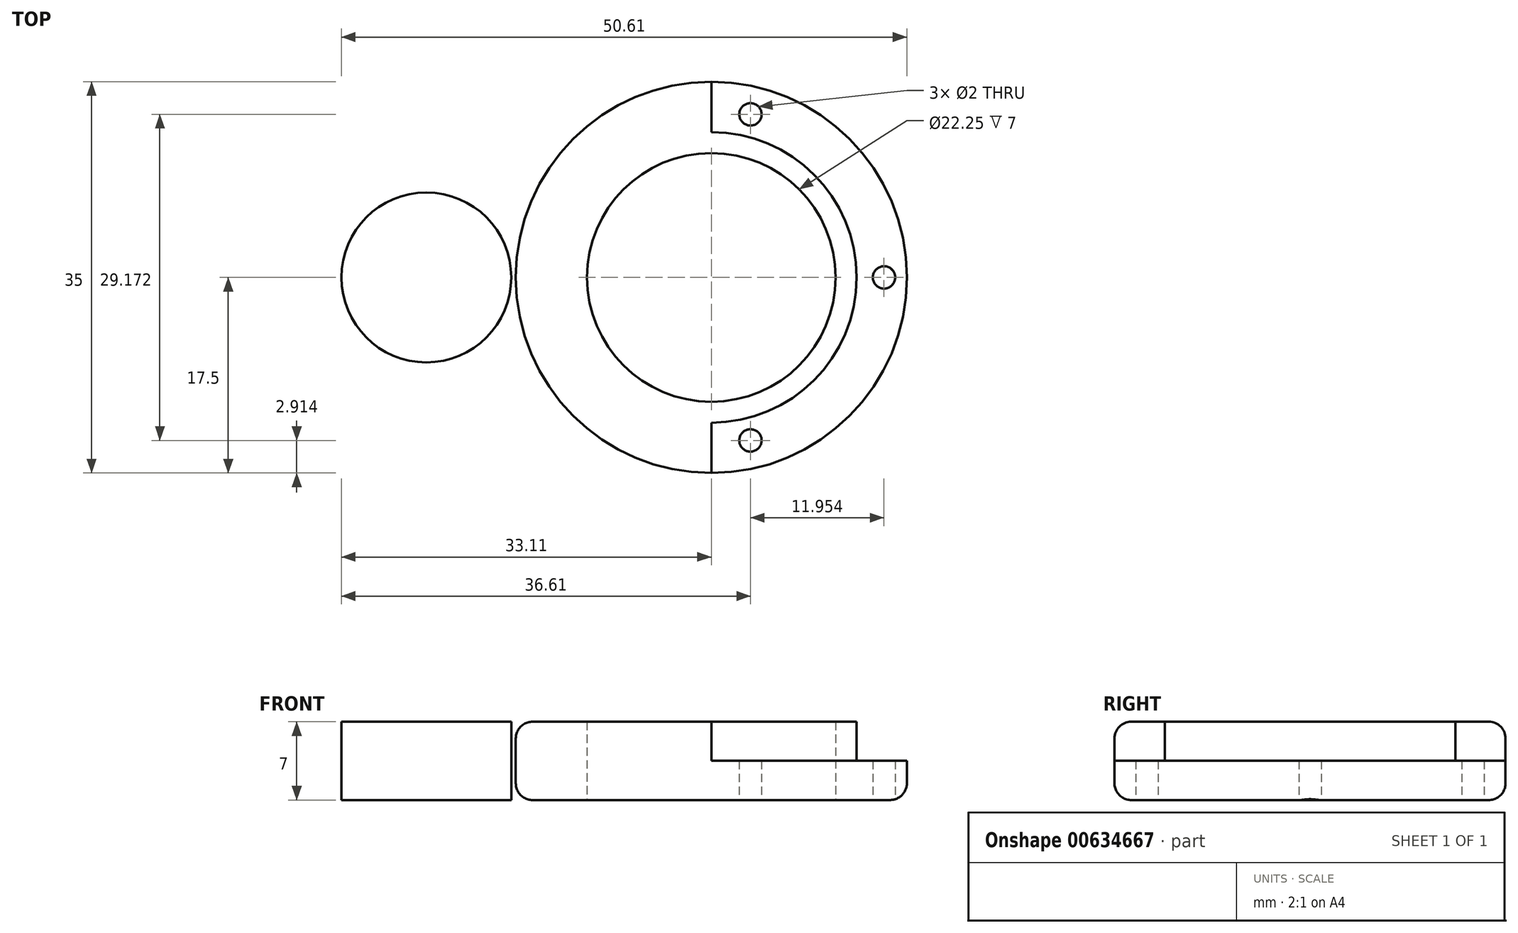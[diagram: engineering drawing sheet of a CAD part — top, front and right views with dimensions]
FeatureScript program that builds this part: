
annotation { "Feature Type Name" : "Feature", "Feature Type Description" : "" }
export const myFeature = defineFeature(function(context is Context, id is Id, definition is map)
    precondition{}
    {
        {
            var Q0;
            Q0=qCreatedBy(makeId("Top.planeOp"),FACE);
            var sketch = newSketch(context, id + "F0", { "sketchPlane" : qUnion([Q0])});
            skCircle(sketch, "E0", {"center": v(0, 0) * mm, "radius": 11.12 * mm});
            skCircle(sketch, "E1", {"center": v(0, 0) * mm, "radius": 17.5 * mm});
            skLineSegment(sketch, "E2", {"start": v(0, 0) * mm, "end": v(34.83, 0) * mm, "construction": true});
            skCircle(sketch, "E3", {"center": v(25.5, 0) * mm, "radius": 7.6 * mm});
            skArc(sketch, "E4", {"start": v(21.65, -11.36) * mm, "mid": v(37.5, 0) * mm, "end": v(21.65, 11.36) * mm});
            skArc(sketch, "E5", {"start": v(23.21, -11.78) * mm, "mid": v(17.5, -11.12) * mm, "end": v(11.98, -12.75) * mm});
            skArc(sketch, "E6.MirrorCS", {"start": v(23.21, 11.78) * mm, "mid": v(17.5, 11.12) * mm, "end": v(11.98, 12.75) * mm});
            skLineSegment(sketch, "E7.MirrorCS", {"start": v(0, 0) * mm, "end": v(-34.83, 0) * mm, "construction": true});
            skCircle(sketch, "E8.MirrorC", {"center": v(-25.5, 0) * mm, "radius": 7.6 * mm});
            skArc(sketch, "E9.MirrorC", {"start": v(-21.65, -11.36) * mm, "mid": v(-37.5, 0) * mm, "end": v(-21.65, 11.36) * mm});
            skArc(sketch, "E10.MirrorCS", {"start": v(-23.21, -11.78) * mm, "mid": v(-17.5, -11.12) * mm, "end": v(-11.98, -12.75) * mm});
            skArc(sketch, "E11.MirrorCS", {"start": v(-23.21, 11.78) * mm, "mid": v(-17.5, 11.12) * mm, "end": v(-11.98, 12.75) * mm});
            skCircle(sketch, "E12", {"center": v(3.5, 14.59) * mm, "radius": 0.75 * mm});
            skPoint(sketch, "E13.endSnap0", {"position": v(0, -14.75) * mm});
            skCircle(sketch, "E14", {"center": v(0, 0) * mm, "radius": 13 * mm});
            skCircle(sketch, "E15", {"center": v(3.5, 14.59) * mm, "radius": 1 * mm});
            skCircle(sketch, "E16.MirrorC", {"center": v(3.5, -14.59) * mm, "radius": 1 * mm});
            skCircle(sketch, "E17.MirrorC", {"center": v(3.5, -14.59) * mm, "radius": 0.75 * mm});
            skLineSegment(sketch, "E18", {"start": v(0, 13) * mm, "end": v(0, 17.5) * mm});
            skLineSegment(sketch, "E19", {"start": v(0, -17.5) * mm, "end": v(0, -13) * mm});
            skLineSegment(sketch, "E20", {"start": v(13, 0) * mm, "end": v(17.9, 0) * mm, "construction": true});
            skCircle(sketch, "E21.MirrorC", {"center": v(15.45, 0) * mm, "radius": 1 * mm});
            skCircle(sketch, "E22.MirrorC", {"center": v(15.45, 0) * mm, "radius": 0.75 * mm});
            skSolve(sketch);
        }
        {
            var Q0;
            {var subQ0=sQuery(id+"F0.wireOp",EDGE,"E18");Q0=makeQuery(id+"F0.imprint","IMPRINT",FACE,{"disambiguationData":[TD([[makeQuery(id+"F0.imprint","IMPRINT",EDGE,{"derivedFrom":subQ0}),1.0]])]});}
            var Q1;
            Q1=makeQuery(id+"F0.imprint","IMPRINT",FACE,{"disambiguationData":[TD([[makeQuery(id+"F0.imprint","IMPRINT",EDGE,{"derivedFrom":sQuery(id+"F0.wireOp",EDGE,"E8.MirrorC")}),1.0]])]});
            var Q2;
            Q2=makeQuery(id+"F0.imprint","IMPRINT",FACE,{"disambiguationData":[TD([[makeQuery(id+"F0.imprint","IMPRINT",EDGE,{"derivedFrom":sQuery(id+"F0.wireOp",EDGE,"E0")}),-1.0]])]});
            extrude(context, id + "F1", {"entities" : qUnion([Q0, Q1, Q2]), "depth" : 7 * mm, "offsetDistance" : 25 * mm});
        }
        {
            var Q0;
            Q0=makeQuery(id+"F0.imprint","IMPRINT",FACE,{"disambiguationData":[TD([[makeQuery(id+"F0.imprint","IMPRINT",EDGE,{"derivedFrom":sQuery(id+"F0.wireOp",EDGE,"E15")}),-1.0]])]});
            extrude(context, id + "F2", {"entities" : qUnion([Q0]), "operationType" : NewBodyOperationType.ADD, "depth" : 3.5 * mm, "offsetDistance" : 25 * mm});
        }
        {
            var Q0;
            {var subQ0=sQuery(id+"F0.wireOp",EDGE,"E1");Q0=makeQuery(id+"F1.opExtrude","CAP_EDGE",EDGE,{"disambiguationData":[OSD([subQ0]),TDD([makeQuery(id+"F0.imprint","IMPRINT",EDGE,{"disambiguationData":[TD([[makeQuery(id+"F0.imprint","INTERSECT",VERTEX,{"derivedFrom":[subQ0,sQuery(id+"F0.wireOp",EDGE,"E10.MirrorCS")]}),-1.0]])],"derivedFrom":subQ0})])],"isStart":false});}
            var Q1;
            Q1=makeQuery(id+"F1.opExtrude","CAP_EDGE",EDGE,{"disambiguationData":[OSD([sQuery(id+"F0.wireOp",EDGE,"E10.MirrorCS")])],"isStart":false});
            var Q2;
            Q2=makeQuery(id+"F1.opExtrude","CAP_EDGE",EDGE,{"disambiguationData":[OSD([sQuery(id+"F0.wireOp",EDGE,"E9.MirrorC")])],"isStart":false});
            var Q3;
            Q3=makeQuery(id+"F1.opExtrude","CAP_EDGE",EDGE,{"disambiguationData":[OSD([sQuery(id+"F0.wireOp",EDGE,"E11.MirrorCS")])],"isStart":false});
            var Q4;
            {var subQ0=sQuery(id+"F0.wireOp",EDGE,"E1");Q4=makeQuery(id+"F1.opExtrude","CAP_EDGE",EDGE,{"disambiguationData":[OSD([subQ0]),TDD([makeQuery(id+"F0.imprint","IMPRINT",EDGE,{"disambiguationData":[TD([[makeQuery(id+"F0.imprint","INTERSECT",VERTEX,{"derivedFrom":[subQ0,sQuery(id+"F0.wireOp",EDGE,"E11.MirrorCS")]}),1.0]])],"derivedFrom":subQ0})])],"isStart":false});}
            var Q5;
            Q5=makeQuery(id+"F1.opExtrude","CAP_EDGE",EDGE,{"disambiguationData":[OSD([sQuery(id+"F0.wireOp",EDGE,"E11.MirrorCS")])],"isStart":true});
            var Q6;
            Q6=makeQuery(id+"F1.opExtrude","CAP_EDGE",EDGE,{"disambiguationData":[OSD([sQuery(id+"F0.wireOp",EDGE,"E9.MirrorC")])],"isStart":true});
            var Q7;
            Q7=makeQuery(id+"F1.opExtrude","CAP_EDGE",EDGE,{"disambiguationData":[OSD([sQuery(id+"F0.wireOp",EDGE,"E10.MirrorCS")])],"isStart":true});
            var Q8;
            {var subQ0=sQuery(id+"F0.wireOp",EDGE,"E1");Q8=makeQuery(id+"F2.boolean.opBoolean","MERGE",EDGE,{"derivedFrom":[makeQuery(id+"F1.opExtrude","CAP_EDGE",EDGE,{"disambiguationData":[OSD([subQ0]),TDD([makeQuery(id+"F0.imprint","IMPRINT",EDGE,{"disambiguationData":[TD([[makeQuery(id+"F0.imprint","INTERSECT",VERTEX,{"derivedFrom":[subQ0,sQuery(id+"F0.wireOp",EDGE,"E11.MirrorCS")]}),1.0]])],"derivedFrom":subQ0})])],"isStart":true}),makeQuery(id+"F1.opExtrude","CAP_EDGE",EDGE,{"disambiguationData":[OSD([subQ0]),TDD([makeQuery(id+"F0.imprint","IMPRINT",EDGE,{"disambiguationData":[TD([[makeQuery(id+"F0.imprint","INTERSECT",VERTEX,{"derivedFrom":[subQ0,sQuery(id+"F0.wireOp",EDGE,"E10.MirrorCS")]}),-1.0]])],"derivedFrom":subQ0})])],"isStart":true}),makeQuery(id+"F2.opExtrude","CAP_EDGE",EDGE,{"disambiguationData":[OSD([subQ0])],"isStart":true})]});}
            fillet(context, id + "F3", {"entities" : qUnion([Q0, Q1, Q2, Q3, Q4, Q5, Q6, Q7, Q8]), "radius" : 1.5 * mm, "tangentPropagation" : true, "allowEdgeOverflow" : false});
        }
    });
